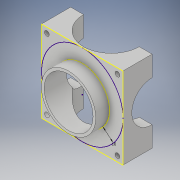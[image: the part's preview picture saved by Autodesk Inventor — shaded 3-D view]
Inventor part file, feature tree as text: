
AUTODESK INVENTOR PART (.ipt)
format: ipt  version: 2019 (Build 230136000, 136)  size: 207,872 bytes
history: native  units: mm
features: sketch x8, extrude x7, projected_geometry x6, pattern_circular x1
ambient origin geometry x8: Origin, YZ Plane, XZ Plane, XY Plane, X Axis, Y Axis, Z Axis, Center Point
bodies: Solid1 (feature_tree)
feature tree (22):
  extrude  "Extrusion1"  Depth=60.0mm
  extrude  "Extrusion2"  Depth=36.0mm
  extrude  "Extrusion3"  Depth=30.0mm
  extrude  "Extrusion4"  Depth=21.5mm
  extrude  "Extrusion5"  Depth=43.0mm
  extrude  "Extrusion6"  Depth=41.0mm
  pattern_circular  "Circular Pattern1"  Count=6  [1 undecoded]
  extrude  "Extrusion7"  Depth=21.5mm
  sketch  "Sketch13"  dims[d18=30.0mm d19=430.0mm d20=0.0mm d21=2.0mm d22=10.0mm d23=0.0mm d24=3.5mm d25=4.0mm d26=4.0mm d27=500.0mm d28=0.0mm d29=40.0mm d30=360.0deg d32=21.5mm d33=0.0mm d55=10.0mm]
  sketch  "Sketch1"  dims[d0=60.0mm d1=60.0mm]
  sketch  "Sketch2"  dims[d2=43.0mm d3=0.0mm d4=36.0mm]
  sketch  "Sketch3"  dims[d5=43.0mm d6=0.0mm d7=30.0mm]
  projected_geometry  "Projected Loop1"
  sketch  "Sketch4"  dims[d8=21.5mm d9=30.0mm]
  projected_geometry  "Projected Loop2"
  sketch  "Sketch5"  dims[d10=60.0mm d11=43.0mm]
  projected_geometry  "Projected Loop3"
  sketch  "Sketch6"  dims[d12=430.0mm d13=0.0mm d14=41.0mm d15=60.0mm]
  projected_geometry  "Projected Loop4"
  sketch  "Sketch7"  dims[d16=43.0mm d17=21.5mm]
  projected_geometry  "Projected Loop5"
  projected_geometry  "Projected Loop11"
note: 1 required parameter value undecoded (feature->parameter linkage not recoverable at this tier; creation-order binding heuristic only, values carry confidence <= 0.55)
